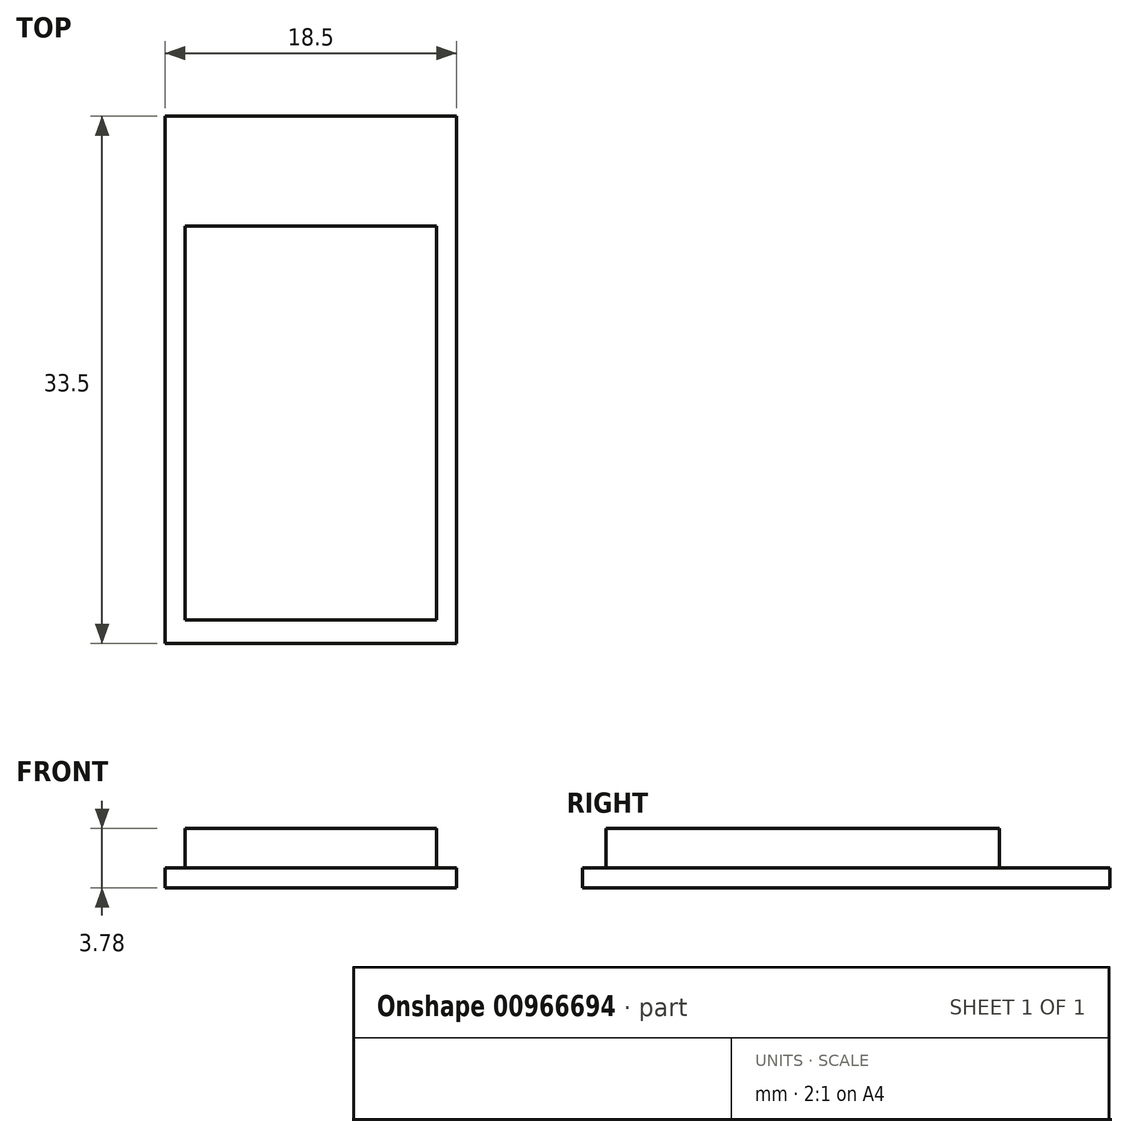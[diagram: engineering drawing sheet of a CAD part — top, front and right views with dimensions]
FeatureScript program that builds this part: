
annotation { "Feature Type Name" : "Feature", "Feature Type Description" : "" }
export const myFeature = defineFeature(function(context is Context, id is Id, definition is map)
    precondition{}
    {
        {
            var Q0;
            Q0=qCreatedBy(makeId("Top.planeOp"),FACE);
            var sketch = newSketch(context, id + "F0", { "sketchPlane" : qUnion([Q0])});
            skLineSegment(sketch, "E0.bottom", {"start": v(9.25, 16.75) * mm, "end": v(-9.25, 16.75) * mm});
            skLineSegment(sketch, "E0.top", {"start": v(9.25, -16.75) * mm, "end": v(-9.25, -16.75) * mm});
            skLineSegment(sketch, "E0.left", {"start": v(9.25, 16.75) * mm, "end": v(9.25, -16.75) * mm});
            skLineSegment(sketch, "E0.right", {"start": v(-9.25, 16.75) * mm, "end": v(-9.25, -16.75) * mm});
            skPoint(sketch, "E0.middle", {"position": v(0, 0) * mm});
            skSolve(sketch);
        }
        {
            var Q0;
            Q0 = qSketchRegion(id + "F0", true);
            extrude(context, id + "F1", {"entities" : qUnion([Q0]), "endBound" : BoundingType.SYMMETRIC, "depth" : 1.27 * mm, "offsetDistance" : 25 * mm});
        }
        {
            var Q0;
            Q0=makeQuery(id+"F1.opExtrude","CAP_FACE",FACE,{"disambiguationData":[OSD([sQuery(id+"F0.wireOp",EDGE,"E0.bottom"),sQuery(id+"F0.wireOp",EDGE,"E0.top"),sQuery(id+"F0.wireOp",EDGE,"E0.left"),sQuery(id+"F0.wireOp",EDGE,"E0.right")])],"isStart":false});
            var sketch = newSketch(context, id + "F2", { "sketchPlane" : qUnion([Q0])});
            skLineSegment(sketch, "E1.bottom", {"start": v(8, -15.25) * mm, "end": v(-8, -15.25) * mm});
            skLineSegment(sketch, "E1.top", {"start": v(8, 9.75) * mm, "end": v(-8, 9.75) * mm});
            skLineSegment(sketch, "E1.left", {"start": v(8, -15.25) * mm, "end": v(8, 9.75) * mm});
            skLineSegment(sketch, "E1.right", {"start": v(-8, -15.25) * mm, "end": v(-8, 9.75) * mm});
            skPoint(sketch, "E1.middle", {"position": v(0, -2.75) * mm});
            skLineSegment(sketch, "E2", {"start": v(0, -15.25) * mm, "end": v(0, -16.75) * mm, "construction": true});
            skSolve(sketch);
        }
        {
            var Q0;
            Q0 = qSketchRegion(id + "F2", true);
            extrude(context, id + "F3", {"entities" : qUnion([Q0]), "depth" : 2.5 * mm, "offsetDistance" : 25 * mm});
        }
    });
